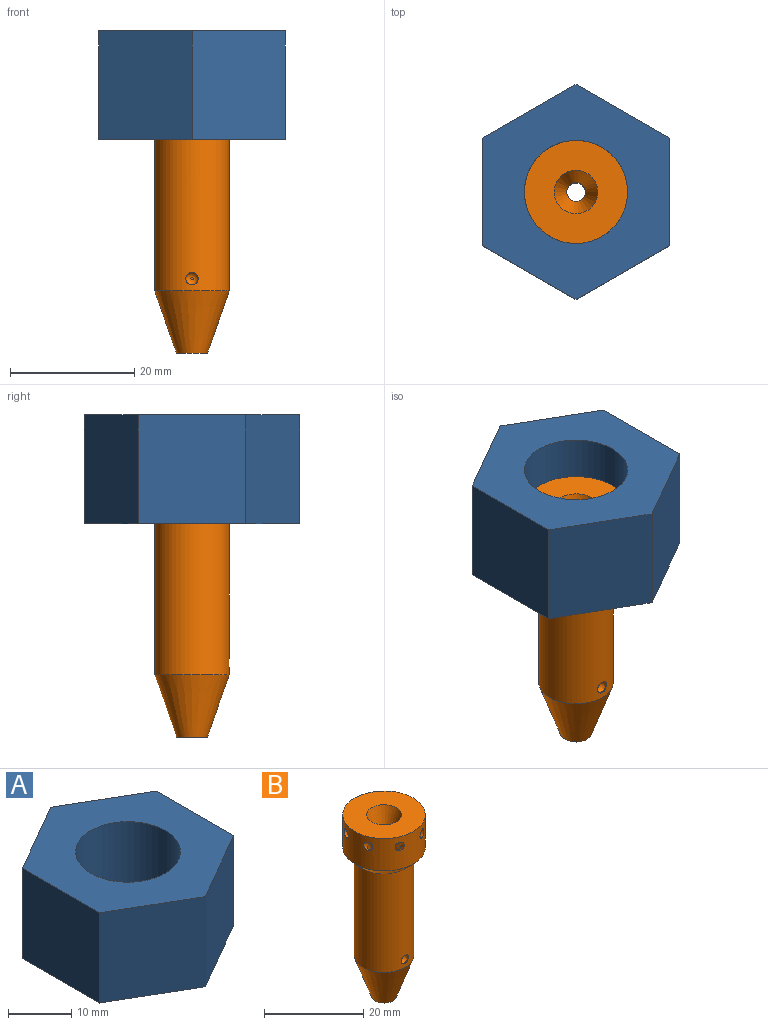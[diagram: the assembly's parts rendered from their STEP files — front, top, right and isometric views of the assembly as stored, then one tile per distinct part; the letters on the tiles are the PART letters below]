
ASSEMBLY  parts=2 mates=1
PART A: 10 faces, bbox 30x34.6x17.5 mm
  f0: plane 17.5x15mm, normal (0.5,-0.87,0), area 303.1mm2, adj f1,f5,f6,f7
  f1: plane 17.5x17.32mm, normal (1,0,0), area 303.1mm2, adj f0,f2,f6,f7
  f2: plane 17.5x15mm, normal (0.5,0.87,0), area 303.1mm2, adj f1,f3,f6,f7
  f3: plane 17.5x15mm, normal (-0.5,0.87,0), area 303.1mm2, adj f2,f4,f6,f7
  f4: plane 17.5x17.32mm, normal (-1,0,0), area 303.1mm2, adj f3,f5,f6,f7
  f5: plane 17.5x15mm, normal (-0.5,-0.87,0), area 303.1mm2, adj f0,f4,f6,f7
  f6: plane 34.64x30mm, normal (0,0,1), area 562.4mm2, adj f0,f1,f2,f3,f4,f5,f8
  f7: plane 34.64x30mm, normal (0,0,-1), area 666.3mm2, adj f0,f1,f2,f3,f4,f5,f9
  f8: cylinder r=8.31mm len=16.62mm, axis (0,0,-1), area 793.2mm2, adj f6,f9
  f9: cone r=6mm half-angle=45deg, axis (0,0,1), area 147mm2, adj f7,f8
PART B: 53 faces, bbox 16.6x16.6x44.7 mm
  f0: cylinder r=6mm len=24.39mm, axis (0,0,1), area 916.3mm2, adj f4,f5,f51
  f1: cone r=1.5mm half-angle=20deg, axis (0,0,1), area 91.9mm2, adj f2,f9
  f2: plane 16.62x16.62mm, normal (0,0,1), area 178.6mm2, adj f1,f3
  f3: cylinder r=8.31mm len=16.62mm, axis (0,0,1), area 392mm2, adj f2,f4,f10,f15,f20,f25,f30,f35
  f4: cone r=6mm half-angle=45deg, axis (0,0,1), area 147mm2, adj f0,f3
  f5: cone r=6mm half-angle=19.3deg, axis (0,0,1), area 282.9mm2, adj f0,f6
  f6: plane 5x5mm, normal (0,0,-1), area 7.1mm2, adj f5,f7
  f7: cylinder r=2mm len=4mm, axis (0,0,1), area 12.6mm2, adj f6,f8
  f8: cone r=2mm half-angle=30deg, axis (0,0,-1), area 11mm2, adj f7,f9
  f9: cylinder r=1.5mm len=37.34mm, axis (0,0,1), area 351.9mm2, adj f1,f8
  f10: torus R=3.29mm, axis (-0.38,0.92,0), area 17.2mm2, adj f3,f13
  f11: cylinder r=1mm len=25.25mm, axis (0,0,1), area 158.7mm2, adj f12,f14
  f12: torus R=10.81mm, axis (-0.38,0.92,0), area 35.6mm2, adj f11,f13
  f13: cylinder r=1mm len=2.62mm, axis (0.46,0.19,0.87), area 11.6mm2, adj f10,f12
  f14: sphere r=1mm, area 6.3mm2, adj f11
  f15: torus R=3.29mm, axis (0.92,-0.38,0), area 17.2mm2, adj f3,f18
  f16: cylinder r=1mm len=25.25mm, axis (0,0,1), area 158.7mm2, adj f17,f19
  f17: torus R=10.81mm, axis (0.92,-0.38,0), area 35.6mm2, adj f16,f18
  f18: cylinder r=1mm len=2.62mm, axis (-0.19,-0.46,0.87), area 11.6mm2, adj f15,f17
  f19: sphere r=1mm, area 6.3mm2, adj f16
  f20: torus R=3.29mm, axis (0.92,0.38,0), area 17.2mm2, adj f3,f23
  f21: cylinder r=1mm len=25.25mm, axis (0,0,1), area 158.7mm2, adj f22,f24
  f22: torus R=10.81mm, axis (0.92,0.38,0), area 35.6mm2, adj f21,f23
  f23: cylinder r=1mm len=2.62mm, axis (0.19,-0.46,0.87), area 11.6mm2, adj f20,f22
  f24: sphere r=1mm, area 6.3mm2, adj f21
  f25: torus R=3.29mm, axis (0.38,0.92,0), area 17.2mm2, adj f3,f28
  f26: cylinder r=1mm len=25.25mm, axis (0,0,1), area 158.7mm2, adj f27,f29
  f27: torus R=10.81mm, axis (0.38,0.92,0), area 35.6mm2, adj f26,f28
  f28: cylinder r=1mm len=2.62mm, axis (0.46,-0.19,0.87), area 11.6mm2, adj f25,f27
  f29: sphere r=1mm, area 6.3mm2, adj f26
  f30: torus R=3.29mm, axis (-0.92,0.38,0), area 17.2mm2, adj f3,f33
  f31: cylinder r=1mm len=25.25mm, axis (0,0,1), area 158.7mm2, adj f32,f34
  f32: torus R=10.81mm, axis (-0.92,0.38,0), area 35.6mm2, adj f31,f33
  f33: cylinder r=1mm len=2.62mm, axis (0.19,0.46,0.87), area 11.6mm2, adj f30,f32
  f34: sphere r=1mm, area 6.3mm2, adj f31
  f35: torus R=3.29mm, axis (-0.92,-0.38,0), area 17.2mm2, adj f3,f38
  f36: cylinder r=1mm len=25.25mm, axis (0,0,1), area 158.7mm2, adj f37,f39
  f37: torus R=10.81mm, axis (-0.92,-0.38,0), area 35.6mm2, adj f36,f38
  f38: cylinder r=1mm len=2.62mm, axis (-0.19,0.46,0.87), area 11.6mm2, adj f35,f37
  f39: sphere r=1mm, area 6.3mm2, adj f36
  f40: torus R=3.29mm, axis (-0.38,-0.92,0), area 17.2mm2, adj f3,f43
  f41: cylinder r=1mm len=25.25mm, axis (0,0,1), area 158.7mm2, adj f42,f44
  f42: torus R=10.81mm, axis (-0.38,-0.92,0), area 35.6mm2, adj f41,f43
  f43: cylinder r=1mm len=2.62mm, axis (-0.46,0.19,0.87), area 11.6mm2, adj f40,f42
  f44: sphere r=1mm, area 6.3mm2, adj f41
  f45: torus R=3.29mm, axis (0.38,-0.92,0), area 17.2mm2, adj f3,f48
  f46: cylinder r=1mm len=25.25mm, axis (0,0,1), area 158.7mm2, adj f47,f49
  f47: torus R=10.81mm, axis (0.38,-0.92,0), area 35.6mm2, adj f46,f48
  f48: cylinder r=1mm len=2.62mm, axis (-0.46,-0.19,0.87), area 11.6mm2, adj f45,f47
  f49: sphere r=1mm, area 6.3mm2, adj f46
  f50: cylinder r=6mm len=0.4mm, axis (0,0,1), area 0.1mm2, adj f52
  f51: cylinder r=1mm len=2mm, axis (0,1,0), area 1mm2, adj f0,f52
  f52: bspline ~2x2mm, area 5.6mm2, adj f50,f51
PLACE A t=(0,0,34.39)mm
PLACE B at identity
MATE revolute A.f9 <-> B.f0  axis (0,0,-1) through (0,0,34.39)mm
